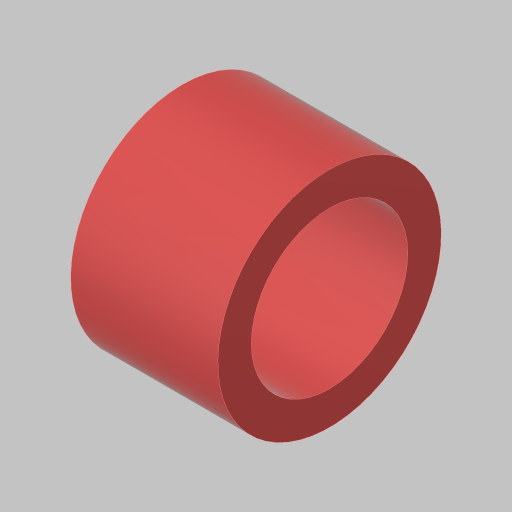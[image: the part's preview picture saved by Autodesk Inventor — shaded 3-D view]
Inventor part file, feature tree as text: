
AUTODESK INVENTOR PART (.ipt)
format: ipt  version: 2023.5 (Build 275446000, 446)  size: 118,784 bytes
history: native  units: in
note: dims shown in document units (in); Inventor stores cm internally (conversion verified against a paired STEP export)
features: extrude x1, sketch x1
ambient origin geometry x8: Origin, YZ Plane, XZ Plane, XY Plane, X Axis, Y Axis, Z Axis, Center Point
bodies: Solid1 (feature_tree)
feature tree (2):
  extrude  "Extrusion1"  Depth=0.55in
  sketch  "Sketch1"  dims[d0=0.585in d1=0.125in d2=0.55in d3=0.0in]
